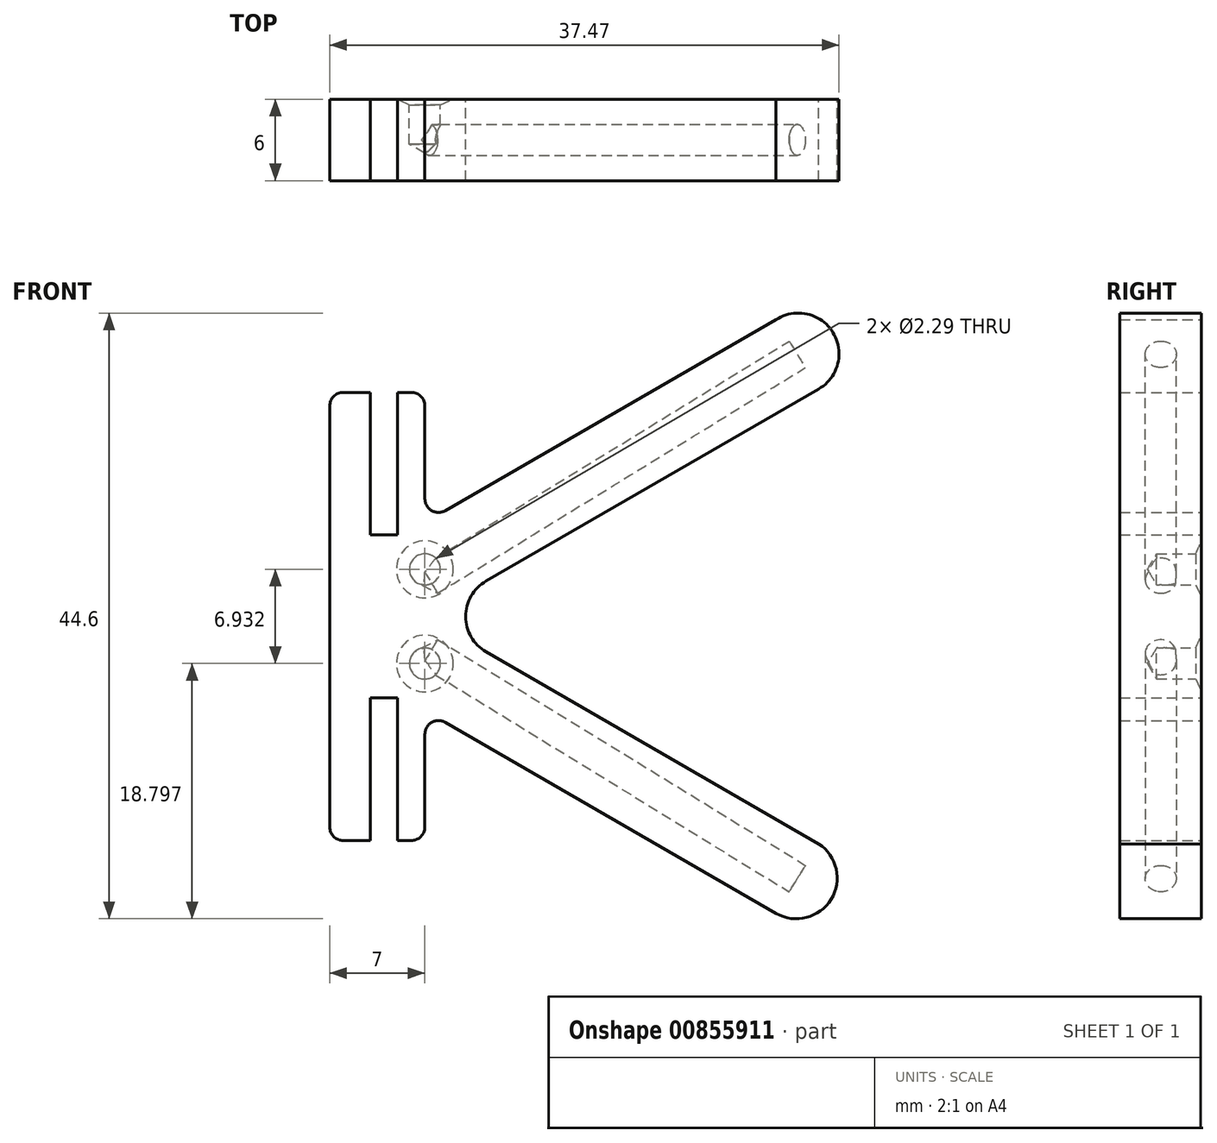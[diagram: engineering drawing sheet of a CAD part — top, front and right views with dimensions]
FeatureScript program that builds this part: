
annotation { "Feature Type Name" : "Feature", "Feature Type Description" : "" }
export const myFeature = defineFeature(function(context is Context, id is Id, definition is map)
    precondition{}
    {
        {
            var Q0;
            Q0=qCreatedBy(makeId("Front.planeOp"),FACE);
            var sketch = newSketch(context, id + "F0", { "sketchPlane" : qUnion([Q0])});
            skLineSegment(sketch, "E0.bottom", {"start": v(1, 6) * mm, "end": v(-1, 6) * mm});
            skLineSegment(sketch, "E0.top", {"start": v(1, -6) * mm, "end": v(-1, -6) * mm});
            skLineSegment(sketch, "E0.left", {"start": v(1, 6) * mm, "end": v(1, -6) * mm});
            skLineSegment(sketch, "E0.right", {"start": v(-1, 6) * mm, "end": v(-1, -6) * mm});
            skPoint(sketch, "E0.middle", {"position": v(0, 0) * mm});
            skLineSegment(sketch, "E1.bottom", {"start": v(-1, -16.5) * mm, "end": v(-3, -16.5) * mm});
            skLineSegment(sketch, "E1.top", {"start": v(-1, 16.5) * mm, "end": v(-3, 16.5) * mm});
            skLineSegment(sketch, "E1.left", {"start": v(-1, -16.5) * mm, "end": v(-1, 16.5) * mm});
            skLineSegment(sketch, "E1.right", {"start": v(-4, -15.5) * mm, "end": v(-4, 15.5) * mm});
            skPoint(sketch, "E1.middle", {"position": v(-2.5, 0) * mm});
            skPoint(sketch, "E2.visualSharp", {"position": v(-4, 16.5) * mm});
            skArc(sketch, "E2.filletArc", {"start": v(-3, 16.5) * mm, "mid": v(-3.7, 16.2) * mm, "end": v(-4, 15.5) * mm});
            skPoint(sketch, "E3.visualSharp", {"position": v(-4, -16.5) * mm});
            skArc(sketch, "E3.filletArc", {"start": v(-4, -15.5) * mm, "mid": v(-3.7, -16.2) * mm, "end": v(-3, -16.5) * mm});
            skLineSegment(sketch, "E4.bottom", {"start": v(1, 16.5) * mm, "end": v(2, 16.5) * mm});
            skLineSegment(sketch, "E4.top", {"start": v(1, -16.5) * mm, "end": v(2, -16.5) * mm});
            skLineSegment(sketch, "E4.left", {"start": v(1, 16.5) * mm, "end": v(1, -16.5) * mm});
            skLineSegment(sketch, "E4.right", {"start": v(3, -8.66) * mm, "end": v(3, -15.5) * mm});
            skLineSegment(sketch, "E5.bottom", {"start": v(7.5, 2.6) * mm, "end": v(31.98, 16.74) * mm});
            skLineSegment(sketch, "E5.top", {"start": v(4.5, 7.8) * mm, "end": v(28.83, 21.86) * mm});
            skLineSegment(sketch, "E6.0", {"start": v(4.5, 7.8) * mm, "end": v(28.83, 21.86) * mm, "construction": true});
            skLineSegment(sketch, "E7", {"start": v(0, 0) * mm, "end": v(3, 0) * mm});
            skPoint(sketch, "E7.endSnap0", {"position": v(3, 0) * mm});
            skLineSegment(sketch, "E8.MirrorCS", {"start": v(4.5, -7.8) * mm, "end": v(28.83, -21.86) * mm});
            skLineSegment(sketch, "E9.MirrorCS", {"start": v(4.5, -7.8) * mm, "end": v(28.83, -21.86) * mm, "construction": true});
            skLineSegment(sketch, "E10.MirrorCS", {"start": v(7.5, -2.6) * mm, "end": v(31.98, -16.74) * mm});
            skPoint(sketch, "E11.visualSharp", {"position": v(3, 16.5) * mm});
            skArc(sketch, "E11.filletArc", {"start": v(3, 15.5) * mm, "mid": v(2.7, 16.2) * mm, "end": v(2, 16.5) * mm});
            skPoint(sketch, "E12.visualSharp", {"position": v(3, -16.5) * mm});
            skArc(sketch, "E12.filletArc", {"start": v(2, -16.5) * mm, "mid": v(2.7, -16.2) * mm, "end": v(3, -15.5) * mm});
            skPoint(sketch, "E13.newPointA", {"position": v(3, -6.93) * mm});
            skLineSegment(sketch, "E14", {"start": v(3, 15.5) * mm, "end": v(3, 8.66) * mm});
            skPoint(sketch, "E15.visualSharp", {"position": v(3, 6.93) * mm});
            skArc(sketch, "E16.filletArc", {"start": v(7.5, 2.6) * mm, "mid": v(6, 0) * mm, "end": v(7.5, -2.6) * mm});
            skLineSegment(sketch, "E17", {"start": v(3, 8.66) * mm, "end": v(3, 8.66) * mm});
            skLineSegment(sketch, "E18", {"start": v(28.83, -21.86) * mm, "end": v(31.98, -16.74) * mm, "construction": true});
            skLineSegment(sketch, "E19", {"start": v(31.98, 16.74) * mm, "end": v(28.83, 21.86) * mm, "construction": true});
            skLineSegment(sketch, "E20", {"start": v(4.5, -7.8) * mm, "end": v(7.5, -2.6) * mm, "construction": true});
            skLineSegment(sketch, "E21", {"start": v(7.5, 2.6) * mm, "end": v(4.5, 7.8) * mm, "construction": true});
            skLineSegment(sketch, "E22", {"start": v(30.47, -19.34) * mm, "end": v(3, -3.46) * mm, "construction": true});
            skLineSegment(sketch, "E23", {"start": v(3, 3.47) * mm, "end": v(30.42, 19.27) * mm, "construction": true});
            skPoint(sketch, "E24.orphan", {"position": v(6, -5.2) * mm});
            skPoint(sketch, "E25.orphan", {"position": v(6, 5.2) * mm});
            skPoint(sketch, "E26", {"position": v(3, 3.47) * mm});
            skPoint(sketch, "E27", {"position": v(3, -3.46) * mm});
            skArc(sketch, "E28.filletArc", {"start": v(3, 8.66) * mm, "mid": v(3.5, 7.8) * mm, "end": v(4.5, 7.8) * mm});
            skArc(sketch, "E29.filletArc", {"start": v(4.5, -7.8) * mm, "mid": v(3.5, -7.8) * mm, "end": v(3, -8.66) * mm});
            skLineSegment(sketch, "E30", {"start": v(28.83, -21.86) * mm, "end": v(31.98, -16.74) * mm});
            skLineSegment(sketch, "E31", {"start": v(31.98, 16.74) * mm, "end": v(28.83, 21.86) * mm});
            skArc(sketch, "E32", {"start": v(31.98, 16.74) * mm, "mid": v(33.03, 20.91) * mm, "end": v(28.83, 21.86) * mm});
            skArc(sketch, "E33", {"start": v(28.83, -21.86) * mm, "mid": v(32.9, -20.83) * mm, "end": v(31.98, -16.74) * mm});
            skSolve(sketch);
        }
        {
            var Q0;
            {var subQ4=sQuery(id+"F0.wireOp",EDGE,"E4.bottom");Q0=makeQuery(id+"F0.imprint","IMPRINT",FACE,{"disambiguationData":[TD([[makeQuery(id+"F0.imprint","IMPRINT",EDGE,{"derivedFrom":subQ4}),-1.0]])]});}
            var Q1;
            {var subQ3=sQuery(id+"F0.wireOp",EDGE,"E1.bottom");Q1=makeQuery(id+"F0.imprint","IMPRINT",FACE,{"disambiguationData":[TD([[makeQuery(id+"F0.imprint","IMPRINT",EDGE,{"derivedFrom":subQ3}),-1.0]])]});}
            var Q2;
            {var subQ1=sQuery(id+"F0.wireOp",EDGE,"E0.bottom");Q2=makeQuery(id+"F0.imprint","IMPRINT",FACE,{"disambiguationData":[TD([[makeQuery(id+"F0.imprint","IMPRINT",EDGE,{"derivedFrom":subQ1}),1.0]])]});}
            extrude(context, id + "F1", {"entities" : qUnion([Q0, Q1, Q2]), "depth" : 6 * mm, "offsetDistance" : 25.4 * mm});
        }
        {
            var Q0;
            {var subQ6=sQuery(id+"F0.wireOp",EDGE,"E4.bottom");Q0=makeQuery(id+"F0.imprint","IMPRINT",FACE,{"disambiguationData":[TD([[makeQuery(id+"F0.imprint","IMPRINT",EDGE,{"derivedFrom":subQ6}),-1.0]])]});}
            var sketch = newSketch(context, id + "F2", { "sketchPlane" : qUnion([Q0])});
            skSolve(sketch);
        }
        {
            var Q0;
            Q0=sQuery(id+"F0.wireOp",VERTEX,"E27");
            var Q1;
            Q1=makeQuery(id+"F1.opExtrude","SWEPT_BODY",BODY,{"disambiguationData":[OSD([sQuery(id+"F0.wireOp",EDGE,"E0.bottom"),sQuery(id+"F0.wireOp",EDGE,"E0.top"),sQuery(id+"F0.wireOp",EDGE,"E1.bottom"),sQuery(id+"F0.wireOp",EDGE,"E1.top"),sQuery(id+"F0.wireOp",EDGE,"E1.left"),sQuery(id+"F0.wireOp",EDGE,"E1.right"),sQuery(id+"F0.wireOp",EDGE,"E2.filletArc"),sQuery(id+"F0.wireOp",EDGE,"E3.filletArc"),sQuery(id+"F0.wireOp",EDGE,"E4.bottom"),sQuery(id+"F0.wireOp",EDGE,"E4.top"),sQuery(id+"F0.wireOp",EDGE,"E4.left"),sQuery(id+"F0.wireOp",EDGE,"E5.bottom"),sQuery(id+"F0.wireOp",EDGE,"E5.top"),sQuery(id+"F0.wireOp",EDGE,"94xJJlr5-P0ZA-G7nr-fBTz-FOYgkDbFN2UJ"),sQuery(id+"F0.wireOp",EDGE,"E8.MirrorCS"),sQuery(id+"F0.wireOp",EDGE,"52e2ee4f-3219-46f6-b922-30e9a29594ac2.MirrorCS"),sQuery(id+"F0.wireOp",EDGE,"E10.MirrorCS"),sQuery(id+"F0.wireOp",EDGE,"E11.filletArc"),sQuery(id+"F0.wireOp",EDGE,"E12.filletArc"),sQuery(id+"F0.wireOp",EDGE,"E4.right"),sQuery(id+"F0.wireOp",EDGE,"E14"),sQuery(id+"F0.wireOp",EDGE,"E16.filletArc"),sQuery(id+"F0.wireOp",EDGE,"E17")])]});
            hole(context, id + "F3", {"style" : HoleStyle.C_SINK, "endStyle" : HoleEndStyle.BLIND, "oppositeDirection" : true, "holeDiameter" : 2.3 * mm, "cSinkDiameter" : 4.2 * mm, "cSinkAngle" : 131 * degree, "majorDiameter" : 6.35 * mm, "holeDepth" : 3.3 * mm, "isTappedThrough" : true, "tappedDepth" : 12.7 * mm, "tapClearance" : 3, "startFromSketch" : true, "locations" : qUnion([Q0]), "scope" : qUnion([Q1])});
        }
        {
            var Q0;
            Q0=sQuery(id+"F0.wireOp",VERTEX,"E26");
            var Q1;
            Q1=makeQuery(id+"F1.opExtrude","SWEPT_BODY",BODY,{"disambiguationData":[OSD([sQuery(id+"F0.wireOp",EDGE,"E0.bottom"),sQuery(id+"F0.wireOp",EDGE,"E0.top"),sQuery(id+"F0.wireOp",EDGE,"E1.bottom"),sQuery(id+"F0.wireOp",EDGE,"E1.top"),sQuery(id+"F0.wireOp",EDGE,"E1.left"),sQuery(id+"F0.wireOp",EDGE,"E1.right"),sQuery(id+"F0.wireOp",EDGE,"E2.filletArc"),sQuery(id+"F0.wireOp",EDGE,"E3.filletArc"),sQuery(id+"F0.wireOp",EDGE,"E4.bottom"),sQuery(id+"F0.wireOp",EDGE,"E4.top"),sQuery(id+"F0.wireOp",EDGE,"E4.left"),sQuery(id+"F0.wireOp",EDGE,"E5.bottom"),sQuery(id+"F0.wireOp",EDGE,"E5.top"),sQuery(id+"F0.wireOp",EDGE,"94xJJlr5-P0ZA-G7nr-fBTz-FOYgkDbFN2UJ"),sQuery(id+"F0.wireOp",EDGE,"E8.MirrorCS"),sQuery(id+"F0.wireOp",EDGE,"52e2ee4f-3219-46f6-b922-30e9a29594ac2.MirrorCS"),sQuery(id+"F0.wireOp",EDGE,"E10.MirrorCS"),sQuery(id+"F0.wireOp",EDGE,"E11.filletArc"),sQuery(id+"F0.wireOp",EDGE,"E12.filletArc"),sQuery(id+"F0.wireOp",EDGE,"E4.right"),sQuery(id+"F0.wireOp",EDGE,"E14"),sQuery(id+"F0.wireOp",EDGE,"E16.filletArc"),sQuery(id+"F0.wireOp",EDGE,"E17")])]});
            hole(context, id + "F4", {"style" : HoleStyle.C_SINK, "endStyle" : HoleEndStyle.BLIND, "oppositeDirection" : true, "holeDiameter" : 2.3 * mm, "cSinkDiameter" : 4.2 * mm, "cSinkAngle" : 131 * degree, "majorDiameter" : 6.35 * mm, "holeDepth" : 3.3 * mm, "isTappedThrough" : true, "tappedDepth" : 12.7 * mm, "tapClearance" : 3, "startFromSketch" : true, "locations" : qUnion([Q0]), "scope" : qUnion([Q1])});
        }
        {
            var Q0;
            Q0=makeQuery(id+"F1.opExtrude","SWEPT_FACE",FACE,{"disambiguationData":[OSD([sQuery(id+"F0.wireOp",EDGE,"E31")])]});
            var sketch = newSketch(context, id + "F5", { "sketchPlane" : qUnion([Q0])});
            skLineSegment(sketch, "E34", {"start": v(0, 3.53) * mm, "end": v(-6, -2.47) * mm, "construction": true});
            skLineSegment(sketch, "E35", {"start": v(-6, -2.47) * mm, "end": v(-3, 0.53) * mm, "construction": true});
            skSolve(sketch);
        }
        {
            var Q0;
            Q0=sQuery(id+"F5.wireOp",VERTEX,"E35.end");
            var Q1;
            Q1=makeQuery(id+"F1.opExtrude","SWEPT_BODY",BODY,{"disambiguationData":[OSD([sQuery(id+"F0.wireOp",EDGE,"E0.bottom"),sQuery(id+"F0.wireOp",EDGE,"E0.top"),sQuery(id+"F0.wireOp",EDGE,"E1.bottom"),sQuery(id+"F0.wireOp",EDGE,"E1.top"),sQuery(id+"F0.wireOp",EDGE,"E1.left"),sQuery(id+"F0.wireOp",EDGE,"E1.right"),sQuery(id+"F0.wireOp",EDGE,"E2.filletArc"),sQuery(id+"F0.wireOp",EDGE,"E3.filletArc"),sQuery(id+"F0.wireOp",EDGE,"E4.bottom"),sQuery(id+"F0.wireOp",EDGE,"E4.top"),sQuery(id+"F0.wireOp",EDGE,"E4.left"),sQuery(id+"F0.wireOp",EDGE,"E5.bottom"),sQuery(id+"F0.wireOp",EDGE,"E5.top"),sQuery(id+"F0.wireOp",EDGE,"E8.MirrorCS"),sQuery(id+"F0.wireOp",EDGE,"E10.MirrorCS"),sQuery(id+"F0.wireOp",EDGE,"E11.filletArc"),sQuery(id+"F0.wireOp",EDGE,"E12.filletArc"),sQuery(id+"F0.wireOp",EDGE,"E4.right"),sQuery(id+"F0.wireOp",EDGE,"E14"),sQuery(id+"F0.wireOp",EDGE,"E16.filletArc"),sQuery(id+"F0.wireOp",EDGE,"E28.filletArc"),sQuery(id+"F0.wireOp",EDGE,"E29.filletArc"),sQuery(id+"F0.wireOp",EDGE,"E30"),sQuery(id+"F0.wireOp",EDGE,"E31")])]});
            hole(context, id + "F6", {"style" : HoleStyle.SIMPLE, "endStyle" : HoleEndStyle.BLIND, "holeDiameter" : 2.3 * mm, "majorDiameter" : 6.35 * mm, "holeDepth" : 31.75 * mm, "isTappedThrough" : true, "tappedDepth" : 12.7 * mm, "tapClearance" : 3, "startFromSketch" : true, "locations" : qUnion([Q0]), "scope" : qUnion([Q1])});
        }
        {
            var Q0;
            Q0=makeQuery(id+"F1.opExtrude","SWEPT_FACE",FACE,{"disambiguationData":[OSD([sQuery(id+"F0.wireOp",EDGE,"E30")])]});
            var sketch = newSketch(context, id + "F7", { "sketchPlane" : qUnion([Q0])});
            skLineSegment(sketch, "E36", {"start": v(0, 2.47) * mm, "end": v(-6, -3.53) * mm, "construction": true});
            skLineSegment(sketch, "E37", {"start": v(-6, -3.53) * mm, "end": v(-3, -0.53) * mm, "construction": true});
            skSolve(sketch);
        }
        {
            var Q0;
            Q0=sQuery(id+"F7.wireOp",VERTEX,"E37.end");
            var Q1;
            Q1=makeQuery(id+"F1.opExtrude","SWEPT_BODY",BODY,{"disambiguationData":[OSD([sQuery(id+"F0.wireOp",EDGE,"E0.bottom"),sQuery(id+"F0.wireOp",EDGE,"E0.top"),sQuery(id+"F0.wireOp",EDGE,"E1.bottom"),sQuery(id+"F0.wireOp",EDGE,"E1.top"),sQuery(id+"F0.wireOp",EDGE,"E1.left"),sQuery(id+"F0.wireOp",EDGE,"E1.right"),sQuery(id+"F0.wireOp",EDGE,"E2.filletArc"),sQuery(id+"F0.wireOp",EDGE,"E3.filletArc"),sQuery(id+"F0.wireOp",EDGE,"E4.bottom"),sQuery(id+"F0.wireOp",EDGE,"E4.top"),sQuery(id+"F0.wireOp",EDGE,"E4.left"),sQuery(id+"F0.wireOp",EDGE,"E5.bottom"),sQuery(id+"F0.wireOp",EDGE,"E5.top"),sQuery(id+"F0.wireOp",EDGE,"E8.MirrorCS"),sQuery(id+"F0.wireOp",EDGE,"E10.MirrorCS"),sQuery(id+"F0.wireOp",EDGE,"E11.filletArc"),sQuery(id+"F0.wireOp",EDGE,"E12.filletArc"),sQuery(id+"F0.wireOp",EDGE,"E4.right"),sQuery(id+"F0.wireOp",EDGE,"E14"),sQuery(id+"F0.wireOp",EDGE,"E16.filletArc"),sQuery(id+"F0.wireOp",EDGE,"E28.filletArc"),sQuery(id+"F0.wireOp",EDGE,"E29.filletArc"),sQuery(id+"F0.wireOp",EDGE,"E30"),sQuery(id+"F0.wireOp",EDGE,"E31")])]});
            hole(context, id + "F8", {"style" : HoleStyle.SIMPLE, "endStyle" : HoleEndStyle.BLIND, "holeDiameter" : 2.3 * mm, "majorDiameter" : 6.35 * mm, "holeDepth" : 31.75 * mm, "isTappedThrough" : true, "tappedDepth" : 12.7 * mm, "tapClearance" : 3, "startFromSketch" : true, "locations" : qUnion([Q0]), "scope" : qUnion([Q1])});
        }
        {
            var Q0;
            Q0=makeQuery(id+"F0.imprint","IMPRINT",FACE,{"disambiguationData":[TD([[makeQuery(id+"F0.imprint","IMPRINT",EDGE,{"derivedFrom":sQuery(id+"F0.wireOp",EDGE,"E31")}),-1.0]])]});
            var Q1;
            Q1=makeQuery(id+"F0.imprint","IMPRINT",FACE,{"disambiguationData":[TD([[makeQuery(id+"F0.imprint","IMPRINT",EDGE,{"derivedFrom":sQuery(id+"F0.wireOp",EDGE,"E30")}),-1.0]])]});
            extrude(context, id + "F9", {"entities" : qUnion([Q0, Q1]), "operationType" : NewBodyOperationType.ADD, "depth" : 6 * mm, "offsetDistance" : 25.4 * mm});
        }
    });
